# Revit family: IVLB_PML_LF_Flexcore 1200x300_Plastic
name_source: partatom
category: Lighting Fixtures
units: mm (PartAtom-declared; Revit-internal decimal feet)

## family parameters
Always vertical = Yes
Cut with Voids When Loaded = No
Light Source = Yes
OmniClass Number = 23.80.70.11.11
OmniClass Title = General Luminaries, Non Directional
Part Type = Normal
Room Calculation Point = Yes
Round Connector Dimension = Use Diameter
Shared = No
Work Plane-Based = No

## types (4) — shared parameters
Apparent Load = 39 VA
Assembly Code = 63.0
Color Filter = 16777215
Description = Recessed
Dimming Lamp Color Temperature Shift = <None>
Emit Shape Visible in Rendering = No
Emit from Rectangle Length = 1195 mm
Emit from Rectangle Width = 295 mm
IK Value = IK02
IP Value = IP44
IfcExportAs = IfcLightFixtureType
IfcExportType = USERDEFINED
Lamp = LED
Load Classification = Lighting
Luminaire_Body_Material = Select RGB value
Manufacturer = Pragmalux - Distrilight
Model = Flexcore
Tilt Angle = 90.00°
URL = https://www.pragmalux.com
Voltage = 230 V
Wattage Comments = 39W

## per-type parameters (varying)
| type | Photometric Web File |
| 30x120cm-26-39w-3600-5500lm-3000k-3500k-4000k-3cct-cri90-ugr19-driver_6257515689256 | 30x120cm-26-39w-3600-5500lm-3000k-3500k-4000k-3cct-cri90-ugr19-driver_6257515689256.ies |
| 30x120cm-26-39w-3600-5500lm-3000k-3500k-4000k-3cct-cri90-ugr19-philips-driver_6257515689256 | 30x120cm-26-39w-3600-5500lm-3000k-3500k-4000k-3cct-cri90-ugr19-philips-driver_6257515689256.ies |
| 30x120cm-26-39w-3600-5500lm-3000k-4000k-3cct-cri90-ugr19-universele-driver_6257515689257 | 30x120cm-26-39w-3600-5500lm-3000k-4000k-3cct-cri90-ugr19-universele-driver_6257515689257.ies |
| 30x120cm-26-39w-3600-5500lm-3000k-4000k-3cct-cri90-ugr19-zw-philips-driver_6257515689258 | 30x120cm-26-39w-3600-5500lm-3000k-4000k-3cct-cri90-ugr19-zw-philips-driver_6257515689258.ies |

## geometry (parser evidence)
native form markers: Sweep x7
no freeform markers — native parametric forms only
